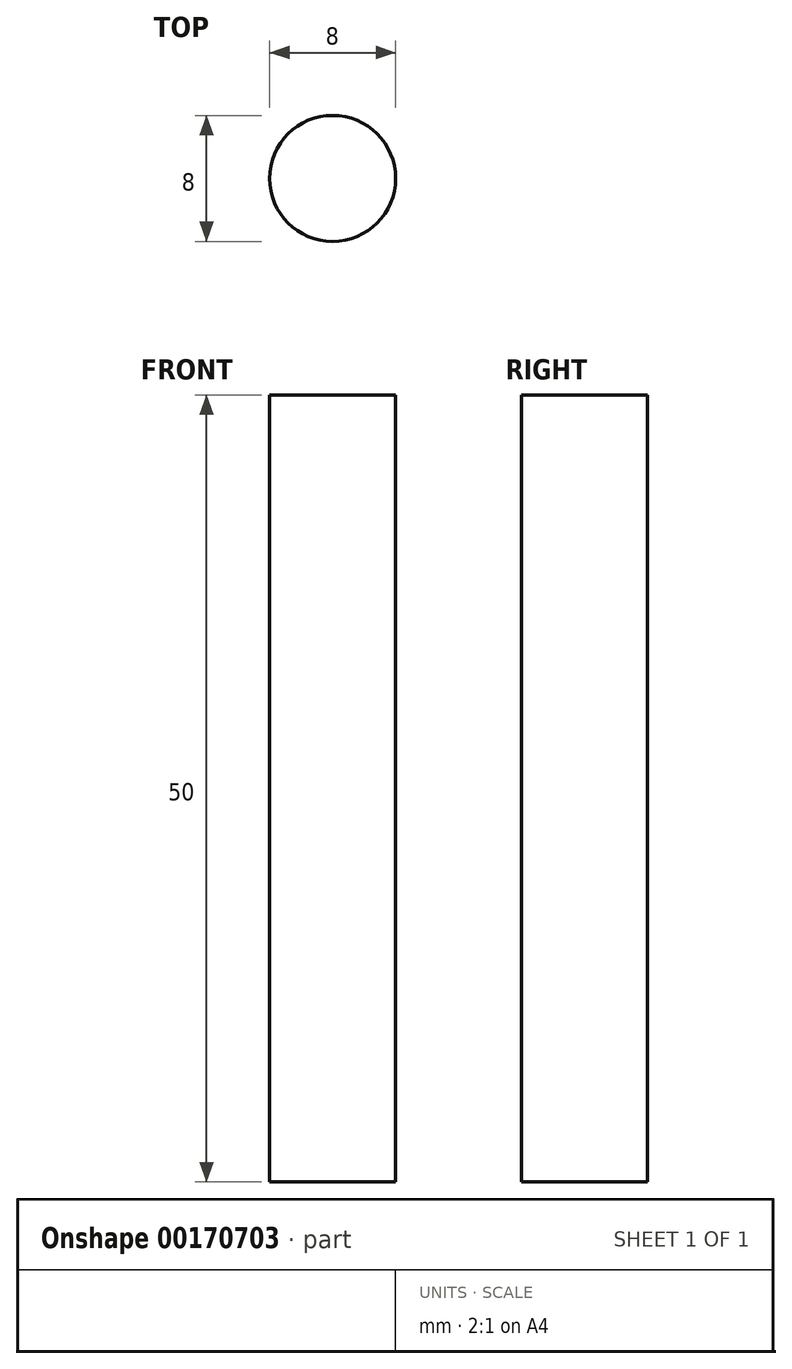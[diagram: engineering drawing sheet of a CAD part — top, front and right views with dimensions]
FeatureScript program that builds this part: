
annotation { "Feature Type Name" : "Feature", "Feature Type Description" : "" }
export const myFeature = defineFeature(function(context is Context, id is Id, definition is map)
    precondition{}
    {
        {
            var Q0;
            Q0=qCreatedBy(makeId("Top.planeOp"),FACE);
            var sketch = newSketch(context, id + "F0", { "sketchPlane" : qUnion([Q0])});
            skCircle(sketch, "E0", {"center": v(0, 0) * mm, "radius": 4 * mm});
            skSolve(sketch);
        }
        {
            var Q0;
            Q0=makeQuery(id+"F0.imprint","IMPRINT",FACE,{"disambiguationData":[TD([[makeQuery(id+"F0.imprint","IMPRINT",EDGE,{"derivedFrom":sQuery(id+"F0.wireOp",EDGE,"E0")}),1.0]])]});
            extrude(context, id + "F1", {"entities" : qUnion([Q0]), "depth" : 50 * mm});
        }
    });
